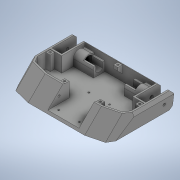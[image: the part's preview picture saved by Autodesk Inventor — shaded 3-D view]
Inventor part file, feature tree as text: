
AUTODESK INVENTOR PART (.ipt)
format: ipt  version: 2020 (Build 240168000, 168)  size: 610,304 bytes
history: native  units: mm
features: extrude x19, sketch x19, projected_geometry x9, chamfer x6, plane x3, mirror x2
ambient origin geometry x8: Origin, YZ Plane, XZ Plane, XY Plane, X Axis, Y Axis, Z Axis, Center Point
bodies: Solid1 (feature_tree)
feature tree (58):
  extrude  "Extrusion1"  Depth=120.0mm
  extrude  "Extrusion2"  TaperAngle=0.0deg  [1 undecoded]
  plane  "Work Plane2"
  extrude  "Extrusion6"  Depth=10.0mm
  plane  "Work Plane4"
  plane  "Work Plane5"
  extrude  "Extrusion7"  TaperAngle=0.0deg  [1 undecoded]
  extrude  "Extrusion8"  Depth=83.204mm TaperAngle=0.0deg
  chamfer  "Chamfer1"  Distance=20.747mm
  chamfer  "Chamfer2"  Distance=27.254mm
  chamfer  "Chamfer3"  Distance=2.0mm Angle=45.0deg
  chamfer  "Chamfer4"  Distance=6.0mm Angle=45.0deg
  chamfer  "Chamfer6"  [1 undecoded]
  extrude  "Extrusion9"  TaperAngle=0.0deg  [1 undecoded]
  extrude  "Extrusion10"  Depth=6.0mm
  extrude  "Extrusion11"  Depth=8.0mm
  extrude  "Extrusion12"  Depth=8.0mm
  mirror  "Mirror2"
  extrude  "WeaponMountSlot"  Depth=8.0mm
  chamfer  "Chamfer7"  Distance=157.438mm
  extrude  "Extrusion14"  Depth=8.0mm
  extrude  "Extrusion15"  Depth=8.0mm TaperAngle=0.0deg
  extrude  "Extrusion16"  Depth=10.0mm TaperAngle=0.0deg
  extrude  "Extrusion17"  Depth=8.0mm
  extrude  "WeaponMountHoles"  Depth=55.8mm
  extrude  "Extrusion19"  Depth=2.0mm TaperAngle=45.0deg
  extrude  "Extrusion20"  Depth=8.0mm
  extrude  "Extrusion21"  Depth=26.0mm
  mirror  "Mirror3"
  extrude  "Extrusion22"  TaperAngle=0.0deg  [1 undecoded]
  sketch  "Sketch1"  dims[d0=180.0mm d1=120.0mm]
  sketch  "Sketch3"  dims[d2=30.0mm d3=0.0mm]
  sketch  "Sketch7"  dims[d4=100.8mm d5=10.0mm]
  projected_geometry  "Projected Loop3"
  sketch  "Sketch9"  dims[d6=10.0mm d7=0.0mm d8=0.0mm]
  sketch  "Sketch10"  dims[d10=45.0deg d18=83.204mm d19=0.0mm d20=20.747mm d21=0.0mm d22=27.254mm d23=0.0mm]
  sketch  "Sketch11"  dims[d24=10.0mm d25=2.0mm d26=45.0deg]
  projected_geometry  "Projected Loop4"
  sketch  "Sketch12"  dims[d27=3.0mm d28=6.0mm d29=45.0deg]
  projected_geometry  "Projected Loop8"
  sketch  "Sketch16"  dims[d30=24.0mm]
  sketch  "Sketch17"  dims[d31=3.0mm]
  sketch  "Sketch18"  dims[d32=45.0deg]
  sketch  "Sketch19"  dims[d33=3.0mm]
  sketch  "Sketch20"  dims[d34=6.0mm]
  projected_geometry  "Projected Loop9"
  projected_geometry  "Projected Loop10"
  projected_geometry  "Projected Loop11"
  projected_geometry  "Projected Loop12"
  sketch  "Sketch21"  dims[d35=45.0deg]
  sketch  "Sketch22"  dims[d39=24.0mm]
  sketch  "Sketch23"  dims[d40=3.0mm]
  sketch  "Sketch24"  dims[d41=45.0deg]
  sketch  "Sketch25"  dims[d45=17.7mm]
  sketch  "Sketch26"  dims[d46=44.25mm d47=0.0mm d48=0.0mm]
  projected_geometry  "Projected Loop13"
  sketch  "Sketch27"  dims[d52=27.0mm d53=0.0mm d58=6.0mm d64=6.5mm d65=16.25mm d66=15.0mm d67=157.438mm d68=0.0mm d69=4.5mm d70=173.156mm d71=0.0mm d72=10.0mm d73=0.0mm d75=37.4mm d76=55.8mm d77=5.0mm d78=2.0mm d79=45.0deg d80=8.0mm d81=26.0mm d82=0.0mm d83=3.75mm d84=3.75mm d85=3.75mm d86=3.75mm d87=7.0mm d88=0.0mm d90=6.0mm d91=4.0mm d92=15.0mm d93=23.0mm d94=7.0mm d95=0.0mm d96=4.0mm d97=15.0mm d98=23.0mm d99=7.0mm d100=0.0mm d101=3.0mm d102=60.0mm d103=3.1mm d104=3.1mm d105=3.1mm d106=3.1mm d107=10.0mm d108=9.4mm d109=9.4mm d110=64.0mm d111=64.0mm d112=9.4mm d113=9.4mm d114=10.0mm d115=27.0mm d116=0.0mm d117=6.1mm d118=0.0mm d119=-7.853982mm d120=16.5mm d121=16.25mm d122=15.0mm d123=2.0mm d124=20.5mm d125=17.0mm d126=0.0mm d127=15.5mm d128=12.2mm d129=19.0mm d130=0.0mm d131=45.0deg d133=19.0mm d134=0.0mm d135=8.0mm d137=6.1mm]
  projected_geometry  "Projected Loop14"
note: 5 required parameter values undecoded (feature->parameter linkage not recoverable at this tier; creation-order binding heuristic only, values carry confidence <= 0.55)
